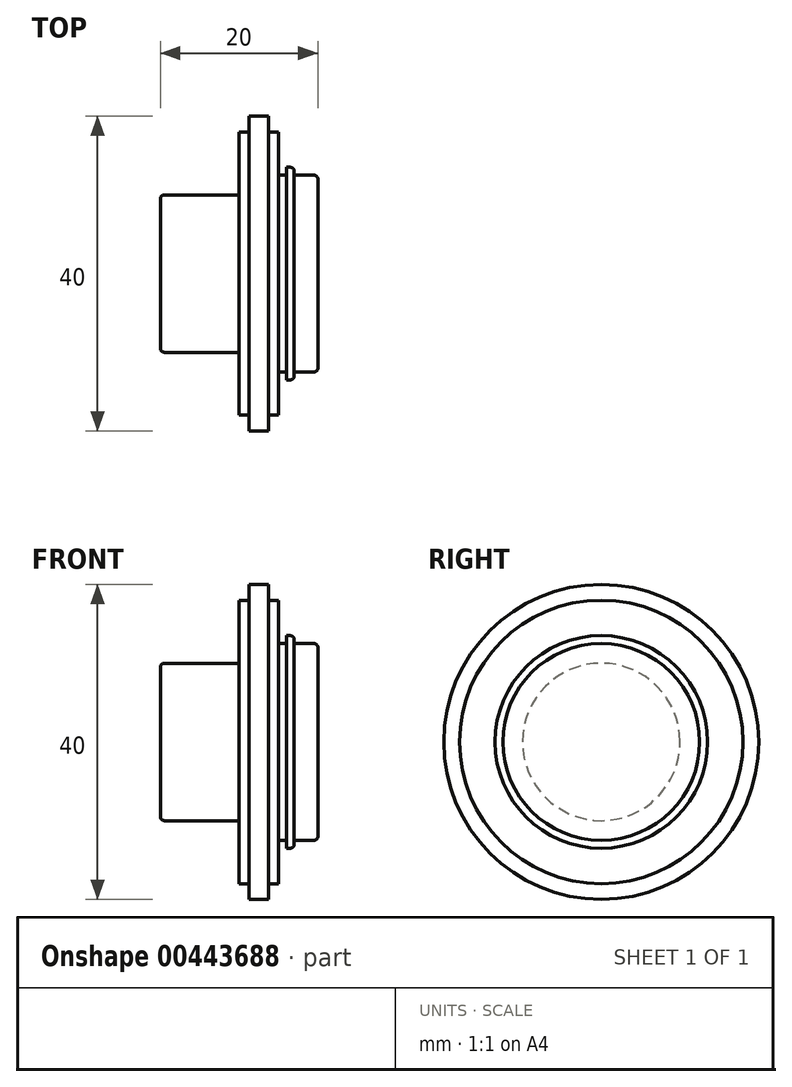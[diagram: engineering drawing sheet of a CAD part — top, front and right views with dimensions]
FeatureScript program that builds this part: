
annotation { "Feature Type Name" : "Feature", "Feature Type Description" : "" }
export const myFeature = defineFeature(function(context is Context, id is Id, definition is map)
    precondition{}
    {
        {
            var Q0;
            Q0=qCreatedBy(makeId("Front.planeOp"),FACE);
            var sketch = newSketch(context, id + "F0", { "sketchPlane" : qUnion([Q0])});
            skLineSegment(sketch, "E0", {"start": v(0, 0) * mm, "end": v(-20, 0) * mm});
            skLineSegment(sketch, "E1", {"start": v(-20, 0) * mm, "end": v(-20, 10) * mm});
            skLineSegment(sketch, "E2", {"start": v(-20, 10) * mm, "end": v(-10, 10) * mm});
            skLineSegment(sketch, "E3", {"start": v(-10, 10) * mm, "end": v(-10, 18) * mm});
            skLineSegment(sketch, "E4", {"start": v(-10, 18) * mm, "end": v(-8.75, 18) * mm});
            skLineSegment(sketch, "E5", {"start": v(-8.75, 18) * mm, "end": v(-8.75, 20) * mm});
            skLineSegment(sketch, "E6", {"start": v(-8.75, 20) * mm, "end": v(-6.25, 20) * mm});
            skLineSegment(sketch, "E7", {"start": v(-6.25, 20) * mm, "end": v(-6.25, 18) * mm});
            skLineSegment(sketch, "E8", {"start": v(-6.25, 18) * mm, "end": v(-5, 18) * mm});
            skLineSegment(sketch, "E9", {"start": v(-5, 18) * mm, "end": v(-5, 12.5) * mm});
            skLineSegment(sketch, "E10", {"start": v(-5, 12.5) * mm, "end": v(-4, 12.5) * mm});
            skLineSegment(sketch, "E11", {"start": v(-4, 12.5) * mm, "end": v(-4, 13.5) * mm});
            skLineSegment(sketch, "E12", {"start": v(-4, 13.5) * mm, "end": v(-3, 13.5) * mm});
            skLineSegment(sketch, "E13", {"start": v(-3, 13.5) * mm, "end": v(-3, 12.5) * mm});
            skLineSegment(sketch, "E14", {"start": v(-3, 12.5) * mm, "end": v(0, 12.5) * mm});
            skLineSegment(sketch, "E15", {"start": v(0, 12.5) * mm, "end": v(0, 0) * mm});
            skSolve(sketch);
        }
        {
            var Q0;
            Q0 = qSketchRegion(id + "F0", true);
            var Q1;
            Q1=sQuery(id+"F0.wireOp",EDGE,"E0");
            revolve(context, id + "F1", {"entities" : qUnion([Q0]), "axis" : qUnion([Q1]), "revolveType" : RevolveType.FULL});
        }
        {
            var Q0;
            Q0=makeQuery(id+"F1.opRevolve","SWEPT_EDGE",EDGE,{"disambiguationData":[OSD([sQuery(id+"F0.wireOp",EDGE,"E1"),sQuery(id+"F0.wireOp",EDGE,"E2")])]});
            var Q1;
            Q1=makeQuery(id+"F1.opRevolve","SWEPT_EDGE",EDGE,{"disambiguationData":[OSD([sQuery(id+"F0.wireOp",EDGE,"E12"),sQuery(id+"F0.wireOp",EDGE,"E13")])]});
            var Q2;
            Q2=makeQuery(id+"F1.opRevolve","SWEPT_EDGE",EDGE,{"disambiguationData":[OSD([sQuery(id+"F0.wireOp",EDGE,"E14"),sQuery(id+"F0.wireOp",EDGE,"E15")])]});
            fillet(context, id + "F2", {"entities" : qUnion([Q0, Q1, Q2]), "radius" : 0.5 * mm, "allowEdgeOverflow" : false});
        }
    });
